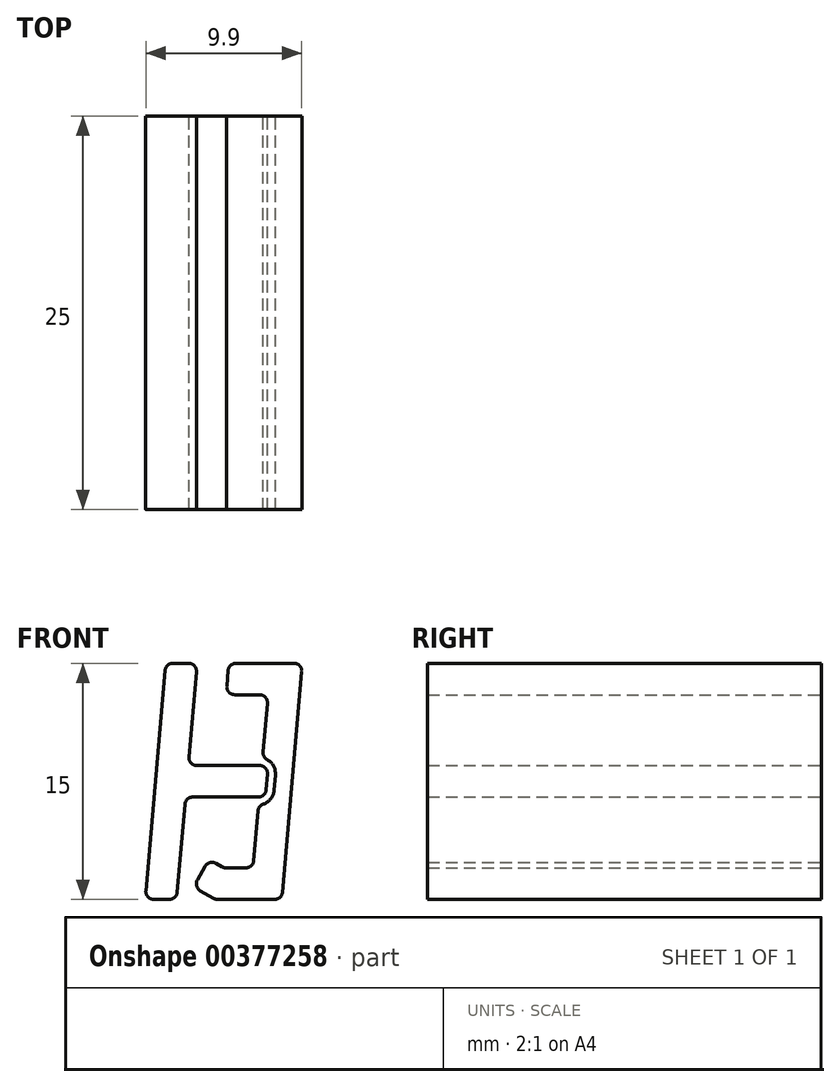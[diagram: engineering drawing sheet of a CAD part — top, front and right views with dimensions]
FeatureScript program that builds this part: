
annotation { "Feature Type Name" : "Feature", "Feature Type Description" : "" }
export const myFeature = defineFeature(function(context is Context, id is Id, definition is map)
    precondition{}
    {
        {
            var Q0;
            Q0=qCreatedBy(makeId("Front.planeOp"),FACE);
            var sketch = newSketch(context, id + "F0", { "sketchPlane" : qUnion([Q0])});
            skLineSegment(sketch, "E0.bottom", {"start": v(5, 7.5) * mm, "end": v(-5, 7.5) * mm, "construction": true});
            skLineSegment(sketch, "E0.top", {"start": v(5, -7.5) * mm, "end": v(-5, -7.5) * mm, "construction": true});
            skLineSegment(sketch, "E0.left", {"start": v(5, 7.5) * mm, "end": v(5, -7.5) * mm, "construction": true});
            skLineSegment(sketch, "E0.right", {"start": v(-5, 7.5) * mm, "end": v(-5, -7.5) * mm, "construction": true});
            skPoint(sketch, "E0.middle", {"position": v(0, 0) * mm});
            skLineSegment(sketch, "E1", {"start": v(-4.95, -6.96) * mm, "end": v(-3.73, 7.04) * mm});
            skLineSegment(sketch, "E2", {"start": v(-3.23, 7.5) * mm, "end": v(-2.23, 7.5) * mm});
            skLineSegment(sketch, "E3", {"start": v(-1.74, 6.96) * mm, "end": v(-2.2, 1.54) * mm});
            skLineSegment(sketch, "E4", {"start": v(-1.71, 1) * mm, "end": v(2.28, 1) * mm});
            skLineSegment(sketch, "E5", {"start": v(2.78, 0.46) * mm, "end": v(2.7, -0.54) * mm});
            skLineSegment(sketch, "E6", {"start": v(2.2, -1) * mm, "end": v(-1.97, -1) * mm});
            skLineSegment(sketch, "E7", {"start": v(-2.47, -1.46) * mm, "end": v(-2.96, -7.04) * mm});
            skLineSegment(sketch, "E8", {"start": v(-3.46, -7.5) * mm, "end": v(-4.45, -7.5) * mm});
            skLineSegment(sketch, "E9", {"start": v(0.78, 7.5) * mm, "end": v(4.45, 7.5) * mm});
            skLineSegment(sketch, "E10", {"start": v(4.95, 6.96) * mm, "end": v(3.73, -7.04) * mm});
            skLineSegment(sketch, "E11", {"start": v(3.23, -7.5) * mm, "end": v(-0.4, -7.5) * mm});
            skLineSegment(sketch, "E12", {"start": v(-0.65, -7.43) * mm, "end": v(-1.5, -6.95) * mm});
            skLineSegment(sketch, "E13", {"start": v(-1.68, -6.26) * mm, "end": v(-1.18, -5.4) * mm});
            skLineSegment(sketch, "E14", {"start": v(-0.5, -5.22) * mm, "end": v(-0.12, -5.43) * mm});
            skLineSegment(sketch, "E15", {"start": v(0.13, -5.5) * mm, "end": v(1.4, -5.5) * mm});
            skLineSegment(sketch, "E16", {"start": v(1.9, -5.04) * mm, "end": v(2.17, -1.88) * mm});
            skLineSegment(sketch, "E17", {"start": v(2.27, 5.5) * mm, "end": v(0.7, 5.5) * mm});
            skLineSegment(sketch, "E18", {"start": v(0.2, 6.04) * mm, "end": v(0.28, 7.04) * mm});
            skLineSegment(sketch, "E19", {"start": v(0, 0) * mm, "end": v(2.74, 0) * mm, "construction": true});
            skPoint(sketch, "E19.endSnap0", {"position": v(2.74, 0) * mm});
            skPoint(sketch, "E20.visualSharp", {"position": v(-3.69, 7.5) * mm});
            skArc(sketch, "E20.filletArc", {"start": v(-3.23, 7.5) * mm, "mid": v(-3.57, 7.37) * mm, "end": v(-3.73, 7.04) * mm});
            skPoint(sketch, "E21.visualSharp", {"position": v(-1.69, 7.5) * mm});
            skArc(sketch, "E22.filletArc", {"start": v(-1.74, 6.96) * mm, "mid": v(-1.86, 7.34) * mm, "end": v(-2.23, 7.5) * mm});
            skPoint(sketch, "E23.visualSharp", {"position": v(-2.26, 1) * mm});
            skArc(sketch, "E23.filletArc", {"start": v(-2.2, 1.54) * mm, "mid": v(-2.08, 1.16) * mm, "end": v(-1.71, 1) * mm});
            skPoint(sketch, "E24.visualSharp", {"position": v(2.83, 1) * mm});
            skArc(sketch, "E24.filletArc", {"start": v(2.78, 0.46) * mm, "mid": v(2.65, 0.84) * mm, "end": v(2.28, 1) * mm});
            skPoint(sketch, "E25.visualSharp", {"position": v(2.65, -1) * mm});
            skArc(sketch, "E25.filletArc", {"start": v(2.2, -1) * mm, "mid": v(2.53, -0.87) * mm, "end": v(2.7, -0.54) * mm});
            skPoint(sketch, "E26.visualSharp", {"position": v(-2.43, -1) * mm});
            skArc(sketch, "E26.filletArc", {"start": v(-1.97, -1) * mm, "mid": v(-2.31, -1.13) * mm, "end": v(-2.47, -1.46) * mm});
            skPoint(sketch, "E27.visualSharp", {"position": v(-3, -7.5) * mm});
            skArc(sketch, "E27.filletArc", {"start": v(-3.46, -7.5) * mm, "mid": v(-3.12, -7.37) * mm, "end": v(-2.96, -7.04) * mm});
            skPoint(sketch, "E28.visualSharp", {"position": v(-5, -7.5) * mm});
            skArc(sketch, "E28.filletArc", {"start": v(-4.95, -6.96) * mm, "mid": v(-4.82, -7.34) * mm, "end": v(-4.45, -7.5) * mm});
            skPoint(sketch, "E29.visualSharp", {"position": v(-1.93, -6.7) * mm});
            skArc(sketch, "E29.filletArc", {"start": v(-1.68, -6.26) * mm, "mid": v(-1.73, -6.64) * mm, "end": v(-1.5, -6.95) * mm});
            skPoint(sketch, "E30.visualSharp", {"position": v(-0.93, -4.97) * mm});
            skArc(sketch, "E30.filletArc", {"start": v(-0.5, -5.22) * mm, "mid": v(-0.87, -5.17) * mm, "end": v(-1.18, -5.4) * mm});
            skPoint(sketch, "E31.visualSharp", {"position": v(0, -5.5) * mm});
            skArc(sketch, "E31.filletArc", {"start": v(-0.12, -5.43) * mm, "mid": v(0, -5.48) * mm, "end": v(0.13, -5.5) * mm});
            skPoint(sketch, "E32.visualSharp", {"position": v(1.86, -5.5) * mm});
            skArc(sketch, "E32.filletArc", {"start": v(1.4, -5.5) * mm, "mid": v(1.73, -5.37) * mm, "end": v(1.9, -5.04) * mm});
            skPoint(sketch, "E33.visualSharp", {"position": v(2.82, 5.5) * mm});
            skArc(sketch, "E33.filletArc", {"start": v(2.77, 4.96) * mm, "mid": v(2.64, 5.34) * mm, "end": v(2.27, 5.5) * mm});
            skPoint(sketch, "E34.visualSharp", {"position": v(0.14, 5.5) * mm});
            skArc(sketch, "E34.filletArc", {"start": v(0.2, 6.04) * mm, "mid": v(0.32, 5.66) * mm, "end": v(0.7, 5.5) * mm});
            skPoint(sketch, "E35.visualSharp", {"position": v(0.32, 7.5) * mm});
            skArc(sketch, "E35.filletArc", {"start": v(0.78, 7.5) * mm, "mid": v(0.44, 7.37) * mm, "end": v(0.28, 7.04) * mm});
            skPoint(sketch, "E36.visualSharp", {"position": v(5, 7.5) * mm});
            skArc(sketch, "E36.filletArc", {"start": v(4.95, 6.96) * mm, "mid": v(4.82, 7.34) * mm, "end": v(4.45, 7.5) * mm});
            skPoint(sketch, "E37.visualSharp", {"position": v(3.69, -7.5) * mm});
            skArc(sketch, "E37.filletArc", {"start": v(3.23, -7.5) * mm, "mid": v(3.57, -7.37) * mm, "end": v(3.73, -7.04) * mm});
            skPoint(sketch, "E38.visualSharp", {"position": v(-0.54, -7.5) * mm});
            skArc(sketch, "E38.filletArc", {"start": v(-0.65, -7.43) * mm, "mid": v(-0.53, -7.48) * mm, "end": v(-0.4, -7.5) * mm});
            skArc(sketch, "E39.1", {"start": v(2.51, -1.45) * mm, "mid": v(2.98, -1.12) * mm, "end": v(3.19, -0.59) * mm});
            skLineSegment(sketch, "E40.0", {"start": v(3.28, 0.41) * mm, "end": v(3.19, -0.59) * mm});
            skArc(sketch, "E41.1", {"start": v(3.28, 0.41) * mm, "mid": v(3.16, 0.97) * mm, "end": v(2.76, 1.38) * mm});
            skLineSegment(sketch, "E42.trimOffspring", {"start": v(2.5, 1.86) * mm, "end": v(2.77, 4.96) * mm});
            skLineSegment(sketch, "E43.trimOffspring", {"start": v(2.25, -1) * mm, "end": v(2.42, 1) * mm});
            skPoint(sketch, "E44.visualSharp", {"position": v(2.2, -1.5) * mm});
            skArc(sketch, "E44.filletArc", {"start": v(2.51, -1.45) * mm, "mid": v(2.28, -1.61) * mm, "end": v(2.17, -1.88) * mm});
            skPoint(sketch, "E45.visualSharp", {"position": v(2.47, 1.48) * mm});
            skArc(sketch, "E45.filletArc", {"start": v(2.5, 1.86) * mm, "mid": v(2.56, 1.58) * mm, "end": v(2.76, 1.38) * mm});
            skSolve(sketch);
        }
        {
            var Q0;
            Q0=qSketchRegion(id+"F0",true);
            extrude(context, id + "F1", {"entities" : qUnion([Q0]), "depth" : 25 * mm});
        }
    });
